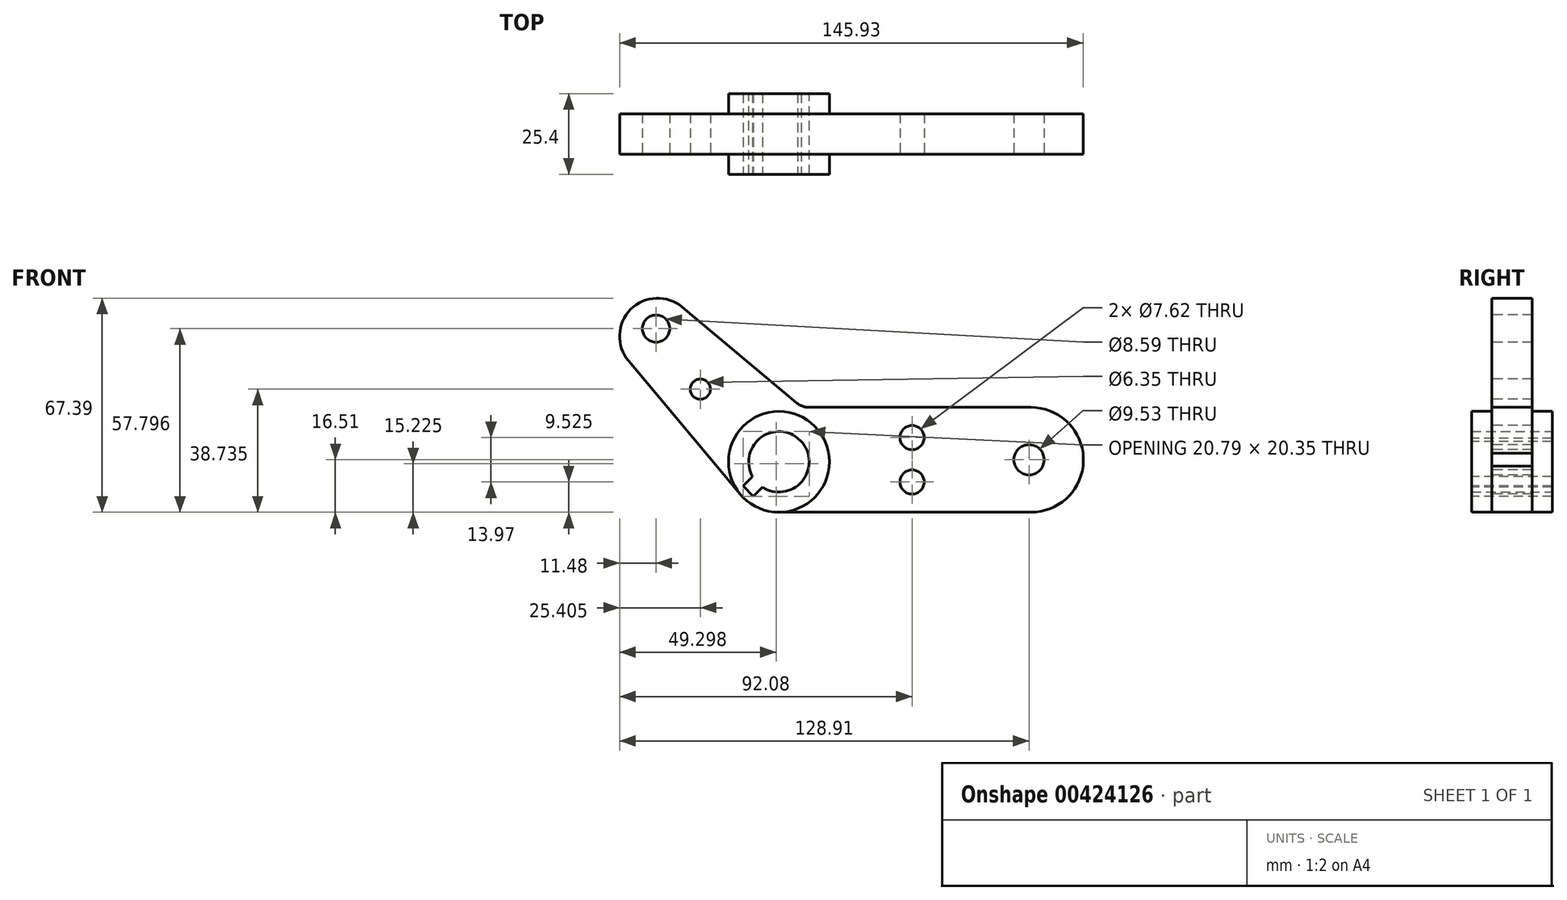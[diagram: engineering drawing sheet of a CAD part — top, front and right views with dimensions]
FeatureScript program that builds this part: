
annotation { "Feature Type Name" : "Feature", "Feature Type Description" : "" }
export const myFeature = defineFeature(function(context is Context, id is Id, definition is map)
    precondition{}
    {
        {
            var Q0;
            Q0=qCreatedBy(makeId("Front.planeOp"),FACE);
            var sketch = newSketch(context, id + "F0", { "sketchPlane" : qUnion([Q0])});
            skLineSegment(sketch, "E0.bottom", {"start": v(0, 0) * mm, "end": v(79.38, 0) * mm});
            skLineSegment(sketch, "E0.top", {"start": v(9.53, 33.02) * mm, "end": v(79.38, 33.02) * mm});
            skArc(sketch, "E1", {"start": v(79.38, 0) * mm, "mid": v(95.89, 16.51) * mm, "end": v(79.38, 33.02) * mm});
            skArc(sketch, "E2", {"start": v(5.44, 34.5) * mm, "mid": v(7.35, 33.4) * mm, "end": v(9.53, 33.02) * mm});
            skArc(sketch, "E3", {"start": v(-12.16, 5.67) * mm, "mid": v(-6.7, 1.49) * mm, "end": v(0, 0) * mm});
            skLineSegment(sketch, "E4", {"start": v(9.53, 39.37) * mm, "end": v(9.53, 33.02) * mm, "construction": true});
            skLineSegment(sketch, "E5", {"start": v(0, 15.88) * mm, "end": v(0, 0) * mm, "construction": true});
            skLineSegment(sketch, "E6", {"start": v(-47.35, 47.6) * mm, "end": v(-12.16, 5.67) * mm});
            skLineSegment(sketch, "E7", {"start": v(-30.38, 64.57) * mm, "end": v(5.44, 34.5) * mm});
            skArc(sketch, "E8", {"start": v(-30.38, 64.57) * mm, "mid": v(-46.64, 63.86) * mm, "end": v(-47.35, 47.6) * mm});
            skPoint(sketch, "E8.third.point", {"position": v(-44.2, 65.73) * mm});
            skLineSegment(sketch, "E9", {"start": v(-50.16, 64.99) * mm, "end": v(-50.16, 10.23) * mm, "construction": true});
            skSolve(sketch);
        }
        {
            var Q0;
            Q0 = qSketchRegion(id + "F0", true);
            extrude(context, id + "F1", {"entities" : qUnion([Q0]), "depth" : 12.7 * mm});
        }
        {
            var Q0;
            Q0=makeQuery(id+"F1.opExtrude","CAP_FACE",FACE,{"disambiguationData":[OSD([sQuery(id+"F0.wireOp",EDGE,"E0.bottom"),sQuery(id+"F0.wireOp",EDGE,"E0.top"),sQuery(id+"F0.wireOp",EDGE,"E1"),sQuery(id+"F0.wireOp",EDGE,"E2"),sQuery(id+"F0.wireOp",EDGE,"E3"),sQuery(id+"F0.wireOp",EDGE,"E6"),sQuery(id+"F0.wireOp",EDGE,"E7"),sQuery(id+"F0.wireOp",EDGE,"E8")])],"isStart":false});
            var sketch = newSketch(context, id + "F2", { "sketchPlane" : qUnion([Q0])});
            skCircle(sketch, "E10", {"center": v(0, 15.88) * mm, "radius": 15.88 * mm});
            skCircle(sketch, "E11", {"center": v(0, 15.88) * mm, "radius": 9.53 * mm});
            skSolve(sketch);
        }
        {
            var Q0;
            Q0 = qSketchRegion(id + "F2", true);
            extrude(context, id + "F3", {"entities" : qUnion([Q0]), "operationType" : NewBodyOperationType.ADD, "depth" : 6.35 * mm, "hasSecondDirection" : true, "secondDirectionOppositeDirection" : true, "secondDirectionDepth" : 19.05 * mm});
        }
        {
            var Q0;
            Q0=makeQuery(id+"F3.boolean.opBoolean","SPLIT",FACE,{"disambiguationData":[TD([makeQuery(id+"F3.opExtrude","SWEPT_FACE",FACE,{"disambiguationData":[OSD([sQuery(id+"F2.wireOp",EDGE,"E11")])]})])],"derivedFrom":makeQuery(id+"F1.opExtrude","CAP_FACE",FACE,{"disambiguationData":[OSD([sQuery(id+"F0.wireOp",EDGE,"E0.bottom"),sQuery(id+"F0.wireOp",EDGE,"E0.top"),sQuery(id+"F0.wireOp",EDGE,"E1"),sQuery(id+"F0.wireOp",EDGE,"E2"),sQuery(id+"F0.wireOp",EDGE,"E3"),sQuery(id+"F0.wireOp",EDGE,"E6"),sQuery(id+"F0.wireOp",EDGE,"E7"),sQuery(id+"F0.wireOp",EDGE,"E8")])],"isStart":false})});
            var sketch = newSketch(context, id + "F4", { "sketchPlane" : qUnion([Q0])});
            skCircle(sketch, "E12.0", {"center": v(0, 15.88) * mm, "radius": 9.53 * mm});
            skSolve(sketch);
        }
        {
            var Q0;
            Q0 = qSketchRegion(id + "F4", true);
            extrude(context, id + "F5", {"entities" : qUnion([Q0]), "operationType" : NewBodyOperationType.REMOVE, "oppositeDirection" : true, "depth" : 25.4 * mm});
        }
        {
            var Q0;
            Q0=makeQuery(id+"F3.opExtrude","CAP_FACE",FACE,{"disambiguationData":[OSD([sQuery(id+"F2.wireOp",EDGE,"E10"),sQuery(id+"F2.wireOp",EDGE,"E11")])],"isStart":false});
            var sketch = newSketch(context, id + "F6", { "sketchPlane" : qUnion([Q0])});
            skLineSegment(sketch, "E13", {"start": v(0, 31.75) * mm, "end": v(0, 0) * mm, "construction": true});
            skLineSegment(sketch, "E14", {"start": v(11, 27.32) * mm, "end": v(-11.45, 4.87) * mm, "construction": true});
            skLineSegment(sketch, "E15", {"start": v(-11.27, 8.28) * mm, "end": v(-8.03, 5.05) * mm});
            skLineSegment(sketch, "E16", {"start": v(-8.03, 5.05) * mm, "end": v(-5.2, 7.9) * mm});
            skLineSegment(sketch, "E17", {"start": v(-11.27, 8.28) * mm, "end": v(-8.32, 11.23) * mm});
            skArc(sketch, "E18.0", {"start": v(-8.32, 11.23) * mm, "mid": v(-6.96, 9.37) * mm, "end": v(-5.2, 7.9) * mm});
            skSolve(sketch);
        }
        {
            var Q0;
            Q0 = qSketchRegion(id + "F6", true);
            extrude(context, id + "F7", {"entities" : qUnion([Q0]), "operationType" : NewBodyOperationType.REMOVE, "endBound" : BoundingType.THROUGH_ALL, "oppositeDirection" : true, "depth" : 25.4 * mm});
        }
        {
            var Q0;
            {var subQ0=sQuery(id+"F0.wireOp",EDGE,"E1");var subQ1=sQuery(id+"F0.wireOp",EDGE,"E0.top");var subQ2=sQuery(id+"F0.wireOp",EDGE,"E2");var subQ3=sQuery(id+"F0.wireOp",EDGE,"E0.bottom");var subQ4=sQuery(id+"F0.wireOp",EDGE,"E3");var subQ5=sQuery(id+"F0.wireOp",EDGE,"E6");var subQ6=sQuery(id+"F0.wireOp",EDGE,"E7");var subQ7=sQuery(id+"F0.wireOp",EDGE,"E8");Q0=makeQuery(id+"F3.boolean.opBoolean","SPLIT",FACE,{"disambiguationData":[TD([makeQuery(id+"F1.opExtrude","SWEPT_FACE",FACE,{"disambiguationData":[OSD([subQ3])]})])],"derivedFrom":makeQuery(id+"F1.opExtrude","CAP_FACE",FACE,{"disambiguationData":[OSD([subQ3,subQ1,subQ0,subQ2,subQ4,subQ5,subQ6,subQ7])],"isStart":false})});}
            var sketch = newSketch(context, id + "F8", { "sketchPlane" : qUnion([Q0])});
            skLineSegment(sketch, "E19", {"start": v(95.89, 16.51) * mm, "end": v(78.74, 16.51) * mm, "construction": true});
            skCircle(sketch, "E20", {"center": v(78.74, 16.51) * mm, "radius": 4.76 * mm});
            skLineSegment(sketch, "E21", {"start": v(95.89, 16.51) * mm, "end": v(41.91, 16.51) * mm, "construction": true});
            skLineSegment(sketch, "E22", {"start": v(41.91, 16.51) * mm, "end": v(41.91, 23.5) * mm, "construction": true});
            skCircle(sketch, "E23", {"center": v(41.91, 23.5) * mm, "radius": 3.81 * mm});
            skCircle(sketch, "E24.MirrorC", {"center": v(41.91, 9.53) * mm, "radius": 3.81 * mm});
            skLineSegment(sketch, "E25", {"start": v(95.89, 16.51) * mm, "end": v(-24.76, 16.51) * mm, "construction": true});
            skLineSegment(sketch, "E26", {"start": v(-24.76, 16.51) * mm, "end": v(-24.76, 38.73) * mm, "construction": true});
            skCircle(sketch, "E27", {"center": v(-24.76, 38.73) * mm, "radius": 3.18 * mm});
            skCircle(sketch, "E28", {"center": v(-38.69, 57.8) * mm, "radius": 4.3 * mm});
            skSolve(sketch);
        }
        {
            var Q0;
            Q0 = qSketchRegion(id + "F8", true);
            extrude(context, id + "F9", {"entities" : qUnion([Q0]), "operationType" : NewBodyOperationType.REMOVE, "endBound" : BoundingType.THROUGH_ALL, "oppositeDirection" : true, "depth" : 25.4 * mm});
        }
        {
            var Q0;
            {var subQ0=sQuery(id+"F0.wireOp",EDGE,"E1");var subQ1=sQuery(id+"F0.wireOp",EDGE,"E0.top");var subQ2=sQuery(id+"F0.wireOp",EDGE,"E2");var subQ3=sQuery(id+"F0.wireOp",EDGE,"E0.bottom");var subQ4=sQuery(id+"F0.wireOp",EDGE,"E3");var subQ5=sQuery(id+"F0.wireOp",EDGE,"E6");var subQ6=sQuery(id+"F0.wireOp",EDGE,"E7");var subQ7=sQuery(id+"F0.wireOp",EDGE,"E8");Q0=makeQuery(id+"F3.boolean.opBoolean","SPLIT",FACE,{"disambiguationData":[TD([makeQuery(id+"F1.opExtrude","SWEPT_FACE",FACE,{"disambiguationData":[OSD([subQ3])]})])],"derivedFrom":makeQuery(id+"F1.opExtrude","CAP_FACE",FACE,{"disambiguationData":[OSD([subQ3,subQ1,subQ0,subQ2,subQ4,subQ5,subQ6,subQ7])],"isStart":false})});}
            var sketch = newSketch(context, id + "F10", { "sketchPlane" : qUnion([Q0])});
            skPoint(sketch, "E29", {"position": v(95.89, 16.51) * mm});
            skSolve(sketch);
        }
        {
            var Q0;
            {var subQ6=sQuery(id+"F0.wireOp",EDGE,"E0.bottom");Q0=makeQuery(id+"F10.imprint","IMPRINT",FACE,{"disambiguationData":[TD([[makeQuery(id+"F10.imprint","IMPRINT",EDGE,{"derivedFrom":makeQuery(id+"F1.opExtrude","CAP_EDGE",EDGE,{"disambiguationData":[OSD([subQ6])],"isStart":false})}),1.0]])]});}
            var sketch = newSketch(context, id + "F11", { "sketchPlane" : qUnion([Q0])});
            skArc(sketch, "E30.0", {"start": v(79.38, 0) * mm, "mid": v(95.89, 16.51) * mm, "end": v(79.38, 33.02) * mm});
            skLineSegment(sketch, "E31.bottom", {"start": v(95.76, 19.05) * mm, "end": v(97.31, 19.05) * mm});
            skLineSegment(sketch, "E31.top", {"start": v(95.76, 13.97) * mm, "end": v(97.31, 13.97) * mm});
            skLineSegment(sketch, "E31.left", {"start": v(95.76, 19.05) * mm, "end": v(95.76, 13.97) * mm});
            skLineSegment(sketch, "E31.right", {"start": v(97.31, 19.05) * mm, "end": v(97.31, 13.97) * mm});
            skSolve(sketch);
        }
        {
            var Q0;
            Q0 = qSketchRegion(id + "F11", true);
            extrude(context, id + "F12", {"entities" : qUnion([Q0]), "operationType" : NewBodyOperationType.REMOVE, "endBound" : BoundingType.THROUGH_ALL, "oppositeDirection" : true, "depth" : 25.4 * mm});
        }
        {
            var Q0;
            Q0=makeQuery(id+"F3.opExtrude","CAP_FACE",FACE,{"disambiguationData":[OSD([sQuery(id+"F2.wireOp",EDGE,"E10"),sQuery(id+"F2.wireOp",EDGE,"E11")])],"isStart":false});
            var sketch = newSketch(context, id + "F13", { "sketchPlane" : qUnion([Q0])});
            skLineSegment(sketch, "E32", {"start": v(-9.65, 6.67) * mm, "end": v(6.5, 22.83) * mm, "construction": true});
            skLineSegment(sketch, "E33", {"start": v(0, 25.4) * mm, "end": v(0, 6.35) * mm, "construction": true});
            skLineSegment(sketch, "E34", {"start": v(7.04, 22.29) * mm, "end": v(5.93, 23.33) * mm});
            skArc(sketch, "E35.trimOffspring", {"start": v(7.04, 22.29) * mm, "mid": v(6.5, 22.83) * mm, "end": v(5.93, 23.33) * mm});
            skPoint(sketch, "E36.trimOffspring.end.orphan", {"position": v(-8.32, 11.23) * mm});
            skPoint(sketch, "E37.0.start.orphan", {"position": v(-5.2, 7.9) * mm});
            skSolve(sketch);
        }
        {
            var Q0;
            Q0 = qSketchRegion(id + "F13", true);
            var Q1;
            Q1=makeQuery(id+"F3.opExtrude","CAP_FACE",FACE,{"disambiguationData":[OSD([sQuery(id+"F2.wireOp",EDGE,"E10"),sQuery(id+"F2.wireOp",EDGE,"E11")])],"isStart":true});
            extrude(context, id + "F14", {"entities" : qUnion([Q0]), "operationType" : NewBodyOperationType.ADD, "oppositeDirection" : true, "endBoundEntityFace" : qUnion([Q1]), "depth" : 25.4 * mm});
        }
    });
